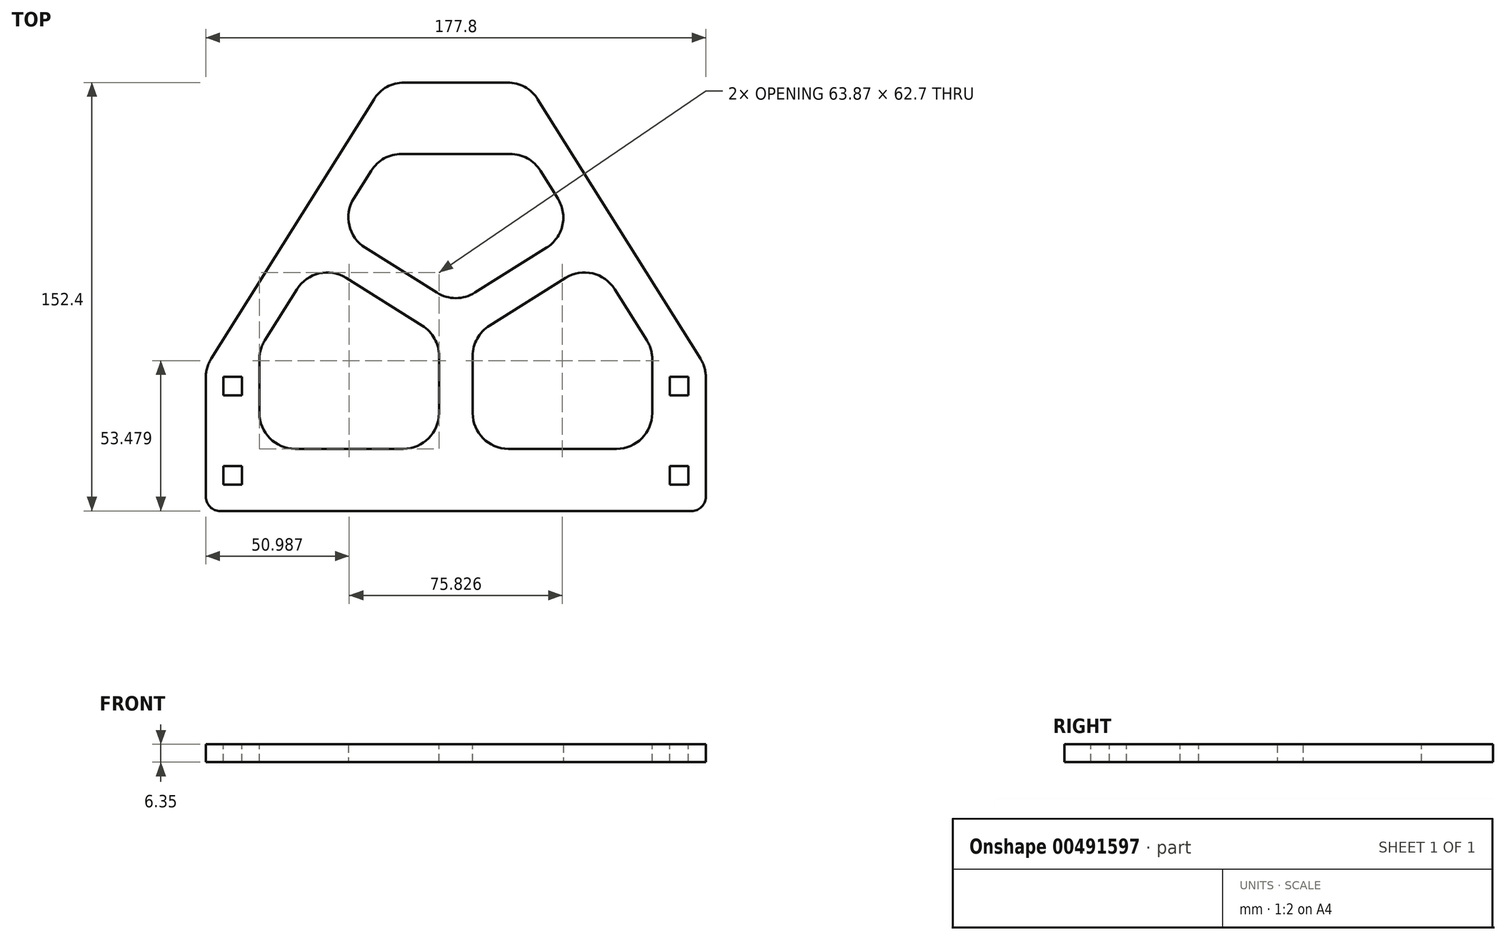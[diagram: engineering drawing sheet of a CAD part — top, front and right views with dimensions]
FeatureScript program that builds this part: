
annotation { "Feature Type Name" : "Feature", "Feature Type Description" : "" }
export const myFeature = defineFeature(function(context is Context, id is Id, definition is map)
    precondition{}
    {
        {
            var Q0;
            Q0=qCreatedBy(makeId("Top.planeOp"),FACE);
            var sketch = newSketch(context, id + "F0", { "sketchPlane" : qUnion([Q0])});
            skLineSegment(sketch, "E0", {"start": v(0, 0) * mm, "end": v(0, 151.3) * mm, "construction": true});
            skLineSegment(sketch, "E1", {"start": v(-188.73, 0) * mm, "end": v(188.13, 0) * mm, "construction": true});
            skLineSegment(sketch, "E2", {"start": v(88.9, 0) * mm, "end": v(88.9, 51.13) * mm});
            skLineSegment(sketch, "E3", {"start": v(88.9, 51.13) * mm, "end": v(25.4, 152.4) * mm});
            skLineSegment(sketch, "E4", {"start": v(-25.4, 152.4) * mm, "end": v(-88.9, 51.13) * mm});
            skLineSegment(sketch, "E5", {"start": v(-88.9, 51.13) * mm, "end": v(-88.9, 0) * mm});
            skLineSegment(sketch, "E6", {"start": v(-25.4, 152.4) * mm, "end": v(0, 152.4) * mm});
            skLineSegment(sketch, "E7", {"start": v(0, 152.4) * mm, "end": v(25.4, 152.4) * mm});
            skLineSegment(sketch, "E8", {"start": v(88.9, 0) * mm, "end": v(0, 0) * mm});
            skLineSegment(sketch, "E9", {"start": v(0, 0) * mm, "end": v(-88.9, 0) * mm});
            skSolve(sketch);
        }
        {
            var Q0;
            Q0 = qSketchRegion(id + "F0", true);
            extrude(context, id + "F1", {"entities" : qUnion([Q0]), "depth" : 6.35 * mm});
        }
        {
            var Q0;
            Q0=makeQuery(id+"F1.opExtrude","CAP_FACE",FACE,{"disambiguationData":[OSD([sQuery(id+"F0.wireOp",EDGE,"E2"),sQuery(id+"F0.wireOp",EDGE,"E3"),sQuery(id+"F0.wireOp",EDGE,"E4"),sQuery(id+"F0.wireOp",EDGE,"E5"),sQuery(id+"F0.wireOp",EDGE,"E6"),sQuery(id+"F0.wireOp",EDGE,"E7"),sQuery(id+"F0.wireOp",EDGE,"E8"),sQuery(id+"F0.wireOp",EDGE,"E9")])],"isStart":false});
            var sketch = newSketch(context, id + "F2", { "sketchPlane" : qUnion([Q0])});
            skLineSegment(sketch, "E10", {"start": v(-57.15, 101.77) * mm, "end": v(78.45, 16.74) * mm, "construction": true});
            skLineSegment(sketch, "E11", {"start": v(57.15, 101.77) * mm, "end": v(-79.95, 15.8) * mm, "construction": true});
            skLineSegment(sketch, "E12", {"start": v(0, 0) * mm, "end": v(0, 142.7) * mm, "construction": true});
            skPoint(sketch, "E12.endSnap0", {"position": v(0, 0) * mm});
            skLineSegment(sketch, "E13", {"start": v(0, 127) * mm, "end": v(-26.34, 127) * mm});
            skLineSegment(sketch, "E14", {"start": v(-26.34, 127) * mm, "end": v(-43.02, 100.4) * mm});
            skLineSegment(sketch, "E15", {"start": v(-43.02, 100.4) * mm, "end": v(0, 73.43) * mm});
            skLineSegment(sketch, "E16", {"start": v(0, 73.43) * mm, "end": v(43.02, 100.4) * mm});
            skLineSegment(sketch, "E17", {"start": v(43.02, 100.4) * mm, "end": v(26.34, 127) * mm});
            skLineSegment(sketch, "E18", {"start": v(26.34, 127) * mm, "end": v(0, 127) * mm});
            skLineSegment(sketch, "E19", {"start": v(-69.85, 22.13) * mm, "end": v(-69.85, 57.6) * mm});
            skLineSegment(sketch, "E20", {"start": v(-69.85, 57.6) * mm, "end": v(-49.76, 89.64) * mm});
            skLineSegment(sketch, "E21", {"start": v(-49.76, 89.64) * mm, "end": v(-5.98, 62.18) * mm});
            skLineSegment(sketch, "E22", {"start": v(-5.98, 62.18) * mm, "end": v(-5.98, 22.13) * mm});
            skLineSegment(sketch, "E23", {"start": v(-5.98, 22.13) * mm, "end": v(-69.85, 22.13) * mm});
            skLineSegment(sketch, "E24", {"start": v(69.85, 22.13) * mm, "end": v(69.85, 57.6) * mm});
            skLineSegment(sketch, "E25", {"start": v(69.85, 57.6) * mm, "end": v(49.76, 89.64) * mm});
            skLineSegment(sketch, "E26", {"start": v(49.76, 89.64) * mm, "end": v(5.98, 62.18) * mm});
            skLineSegment(sketch, "E27", {"start": v(5.98, 62.18) * mm, "end": v(5.98, 22.13) * mm});
            skLineSegment(sketch, "E28", {"start": v(5.98, 22.13) * mm, "end": v(69.85, 22.13) * mm});
            skSolve(sketch);
        }
        {
            var Q0;
            Q0 = qSketchRegion(id + "F2", true);
            extrude(context, id + "F3", {"entities" : qUnion([Q0]), "operationType" : NewBodyOperationType.REMOVE, "oppositeDirection" : true, "depth" : 25.4 * mm});
        }
        {
            var Q0;
            Q0=makeQuery(id+"F1.opExtrude","SWEPT_EDGE",EDGE,{"disambiguationData":[OSD([sQuery(id+"F0.wireOp",EDGE,"E4"),sQuery(id+"F0.wireOp",EDGE,"E6")])]});
            var Q1;
            Q1=makeQuery(id+"F1.opExtrude","SWEPT_EDGE",EDGE,{"disambiguationData":[OSD([sQuery(id+"F0.wireOp",EDGE,"E3"),sQuery(id+"F0.wireOp",EDGE,"E7")])]});
            var Q2;
            Q2=makeQuery(id+"F1.opExtrude","SWEPT_EDGE",EDGE,{"disambiguationData":[OSD([sQuery(id+"F0.wireOp",EDGE,"E2"),sQuery(id+"F0.wireOp",EDGE,"E3")])]});
            var Q3;
            Q3=makeQuery(id+"F1.opExtrude","SWEPT_EDGE",EDGE,{"disambiguationData":[OSD([sQuery(id+"F0.wireOp",EDGE,"E4"),sQuery(id+"F0.wireOp",EDGE,"E5")])]});
            fillet(context, id + "F4", {"entities" : qUnion([Q0, Q1, Q2, Q3]), "radius" : 12.7 * mm, "tangentPropagation" : true, "allowEdgeOverflow" : false});
        }
        {
            var Q0;
            Q0=makeQuery(id+"F3.boolean.opBoolean","COPY",EDGE,{"derivedFrom":makeQuery(id+"F3.opExtrude","SWEPT_EDGE",EDGE,{"disambiguationData":[OSD([sQuery(id+"F2.wireOp",EDGE,"E14"),sQuery(id+"F2.wireOp",EDGE,"E15")])]})});
            var Q1;
            Q1=makeQuery(id+"F3.boolean.opBoolean","COPY",EDGE,{"derivedFrom":makeQuery(id+"F3.opExtrude","SWEPT_EDGE",EDGE,{"disambiguationData":[OSD([sQuery(id+"F2.wireOp",EDGE,"E15"),sQuery(id+"F2.wireOp",EDGE,"E16")])]})});
            var Q2;
            Q2=makeQuery(id+"F3.boolean.opBoolean","COPY",EDGE,{"derivedFrom":makeQuery(id+"F3.opExtrude","SWEPT_EDGE",EDGE,{"disambiguationData":[OSD([sQuery(id+"F2.wireOp",EDGE,"E13"),sQuery(id+"F2.wireOp",EDGE,"E14")])]})});
            var Q3;
            Q3=makeQuery(id+"F3.boolean.opBoolean","COPY",EDGE,{"derivedFrom":makeQuery(id+"F3.opExtrude","SWEPT_EDGE",EDGE,{"disambiguationData":[OSD([sQuery(id+"F2.wireOp",EDGE,"E17"),sQuery(id+"F2.wireOp",EDGE,"E18")])]})});
            var Q4;
            Q4=makeQuery(id+"F3.boolean.opBoolean","COPY",EDGE,{"derivedFrom":makeQuery(id+"F3.opExtrude","SWEPT_EDGE",EDGE,{"disambiguationData":[OSD([sQuery(id+"F2.wireOp",EDGE,"E16"),sQuery(id+"F2.wireOp",EDGE,"E17")])]})});
            var Q5;
            Q5=makeQuery(id+"F3.boolean.opBoolean","COPY",EDGE,{"derivedFrom":makeQuery(id+"F3.opExtrude","SWEPT_EDGE",EDGE,{"disambiguationData":[OSD([sQuery(id+"F2.wireOp",EDGE,"E20"),sQuery(id+"F2.wireOp",EDGE,"E21")])]})});
            var Q6;
            Q6=makeQuery(id+"F3.boolean.opBoolean","COPY",EDGE,{"derivedFrom":makeQuery(id+"F3.opExtrude","SWEPT_EDGE",EDGE,{"disambiguationData":[OSD([sQuery(id+"F2.wireOp",EDGE,"E19"),sQuery(id+"F2.wireOp",EDGE,"E20")])]})});
            var Q7;
            Q7=makeQuery(id+"F3.boolean.opBoolean","COPY",EDGE,{"derivedFrom":makeQuery(id+"F3.opExtrude","SWEPT_EDGE",EDGE,{"disambiguationData":[OSD([sQuery(id+"F2.wireOp",EDGE,"E19"),sQuery(id+"F2.wireOp",EDGE,"E23")])]})});
            var Q8;
            Q8=makeQuery(id+"F3.boolean.opBoolean","COPY",EDGE,{"derivedFrom":makeQuery(id+"F3.opExtrude","SWEPT_EDGE",EDGE,{"disambiguationData":[OSD([sQuery(id+"F2.wireOp",EDGE,"E22"),sQuery(id+"F2.wireOp",EDGE,"E23")])]})});
            var Q9;
            Q9=makeQuery(id+"F3.boolean.opBoolean","COPY",EDGE,{"derivedFrom":makeQuery(id+"F3.opExtrude","SWEPT_EDGE",EDGE,{"disambiguationData":[OSD([sQuery(id+"F2.wireOp",EDGE,"E21"),sQuery(id+"F2.wireOp",EDGE,"E22")])]})});
            var Q10;
            Q10=makeQuery(id+"F3.boolean.opBoolean","COPY",EDGE,{"derivedFrom":makeQuery(id+"F3.opExtrude","SWEPT_EDGE",EDGE,{"disambiguationData":[OSD([sQuery(id+"F2.wireOp",EDGE,"E25"),sQuery(id+"F2.wireOp",EDGE,"E26")])]})});
            var Q11;
            Q11=makeQuery(id+"F3.boolean.opBoolean","COPY",EDGE,{"derivedFrom":makeQuery(id+"F3.opExtrude","SWEPT_EDGE",EDGE,{"disambiguationData":[OSD([sQuery(id+"F2.wireOp",EDGE,"E24"),sQuery(id+"F2.wireOp",EDGE,"E25")])]})});
            var Q12;
            Q12=makeQuery(id+"F3.boolean.opBoolean","COPY",EDGE,{"derivedFrom":makeQuery(id+"F3.opExtrude","SWEPT_EDGE",EDGE,{"disambiguationData":[OSD([sQuery(id+"F2.wireOp",EDGE,"E24"),sQuery(id+"F2.wireOp",EDGE,"E28")])]})});
            var Q13;
            Q13=makeQuery(id+"F3.boolean.opBoolean","COPY",EDGE,{"derivedFrom":makeQuery(id+"F3.opExtrude","SWEPT_EDGE",EDGE,{"disambiguationData":[OSD([sQuery(id+"F2.wireOp",EDGE,"E27"),sQuery(id+"F2.wireOp",EDGE,"E28")])]})});
            var Q14;
            Q14=makeQuery(id+"F3.boolean.opBoolean","COPY",EDGE,{"derivedFrom":makeQuery(id+"F3.opExtrude","SWEPT_EDGE",EDGE,{"disambiguationData":[OSD([sQuery(id+"F2.wireOp",EDGE,"E26"),sQuery(id+"F2.wireOp",EDGE,"E27")])]})});
            fillet(context, id + "F5", {"entities" : qUnion([Q0, Q1, Q2, Q3, Q4, Q5, Q6, Q7, Q8, Q9, Q10, Q11, Q12, Q13, Q14]), "radius" : 12.7 * mm, "tangentPropagation" : true, "allowEdgeOverflow" : false});
        }
        {
            var Q0;
            Q0=makeQuery(id+"F1.opExtrude","CAP_FACE",FACE,{"disambiguationData":[OSD([sQuery(id+"F0.wireOp",EDGE,"E2"),sQuery(id+"F0.wireOp",EDGE,"E3"),sQuery(id+"F0.wireOp",EDGE,"E4"),sQuery(id+"F0.wireOp",EDGE,"E5"),sQuery(id+"F0.wireOp",EDGE,"E6"),sQuery(id+"F0.wireOp",EDGE,"E7"),sQuery(id+"F0.wireOp",EDGE,"E8"),sQuery(id+"F0.wireOp",EDGE,"E9")])],"isStart":false});
            var sketch = newSketch(context, id + "F6", { "sketchPlane" : qUnion([Q0])});
            skLineSegment(sketch, "E29", {"start": v(-79.38, 0) * mm, "end": v(-79.38, 79.94) * mm, "construction": true});
            skLineSegment(sketch, "E30", {"start": v(79.38, 0) * mm, "end": v(79.38, 75.92) * mm, "construction": true});
            skLineSegment(sketch, "E31", {"start": v(-97.1, 12.7) * mm, "end": v(99.38, 12.7) * mm, "construction": true});
            skLineSegment(sketch, "E32", {"start": v(-97.1, 44.45) * mm, "end": v(99.38, 44.45) * mm, "construction": true});
            skLineSegment(sketch, "E33.bottom", {"start": v(-82.68, 47.75) * mm, "end": v(-76.07, 47.75) * mm});
            skLineSegment(sketch, "E33.top", {"start": v(-82.68, 41.15) * mm, "end": v(-76.07, 41.15) * mm});
            skLineSegment(sketch, "E33.left", {"start": v(-82.68, 47.75) * mm, "end": v(-82.68, 41.15) * mm});
            skLineSegment(sketch, "E33.right", {"start": v(-76.07, 47.75) * mm, "end": v(-76.07, 41.15) * mm});
            skPoint(sketch, "E33.middle", {"position": v(-79.38, 44.45) * mm});
            skLineSegment(sketch, "E34.bottom", {"start": v(-82.68, 16) * mm, "end": v(-76.07, 16) * mm});
            skLineSegment(sketch, "E34.top", {"start": v(-82.68, 9.4) * mm, "end": v(-76.07, 9.4) * mm});
            skLineSegment(sketch, "E34.left", {"start": v(-82.68, 16) * mm, "end": v(-82.68, 9.4) * mm});
            skLineSegment(sketch, "E34.right", {"start": v(-76.07, 16) * mm, "end": v(-76.07, 9.4) * mm});
            skPoint(sketch, "E34.middle", {"position": v(-79.38, 12.7) * mm});
            skLineSegment(sketch, "E35.bottom", {"start": v(76.07, 16) * mm, "end": v(82.68, 16) * mm});
            skLineSegment(sketch, "E35.top", {"start": v(76.07, 9.4) * mm, "end": v(82.68, 9.4) * mm});
            skLineSegment(sketch, "E35.left", {"start": v(76.07, 16) * mm, "end": v(76.07, 9.4) * mm});
            skLineSegment(sketch, "E35.right", {"start": v(82.68, 16) * mm, "end": v(82.68, 9.4) * mm});
            skPoint(sketch, "E35.middle", {"position": v(79.38, 12.7) * mm});
            skLineSegment(sketch, "E36.bottom", {"start": v(76.07, 47.75) * mm, "end": v(82.68, 47.75) * mm});
            skLineSegment(sketch, "E36.top", {"start": v(76.07, 41.15) * mm, "end": v(82.68, 41.15) * mm});
            skLineSegment(sketch, "E36.left", {"start": v(76.07, 47.75) * mm, "end": v(76.07, 41.15) * mm});
            skLineSegment(sketch, "E36.right", {"start": v(82.68, 47.75) * mm, "end": v(82.68, 41.15) * mm});
            skPoint(sketch, "E36.middle", {"position": v(79.38, 44.45) * mm});
            skSolve(sketch);
        }
        {
            var Q0;
            Q0 = qSketchRegion(id + "F6", true);
            extrude(context, id + "F7", {"entities" : qUnion([Q0]), "operationType" : NewBodyOperationType.REMOVE, "oppositeDirection" : true, "depth" : 25.4 * mm});
        }
        {
            var Q0;
            Q0=makeQuery(id+"F1.opExtrude","SWEPT_EDGE",EDGE,{"disambiguationData":[OSD([sQuery(id+"F0.wireOp",EDGE,"E5"),sQuery(id+"F0.wireOp",EDGE,"E9")])]});
            var Q1;
            Q1=makeQuery(id+"F1.opExtrude","SWEPT_EDGE",EDGE,{"disambiguationData":[OSD([sQuery(id+"F0.wireOp",EDGE,"E2"),sQuery(id+"F0.wireOp",EDGE,"E8")])]});
            fillet(context, id + "F8", {"entities" : qUnion([Q0, Q1]), "radius" : 5.08 * mm, "tangentPropagation" : true, "allowEdgeOverflow" : false});
        }
    });
